# Revit family: QF_U-Line_UCRE427-SS01A___
name_source: partatom
category: Specialty Equipment
revit_build: Autodesk Revit 2018 (Build: 20190510_1515(x64)
units: mm (PartAtom-declared; Revit-internal decimal feet)

## family parameters
Always vertical = Yes
Cut with Voids When Loaded = No
Part Type = Normal
Room Calculation Point = No
Round Connector Dimension = Use Diameter
Shared = No
Work Plane-Based = No

## types (2) — shared parameters
Accessory = No
BTUH = 1421 W
CE Approved = Yes
Cooling Capacity = 0 kW
Cycle = 60 Hz
D5 = 5 mm  [stored 0.0164042 ft]
Depth Actual = 800 mm  [stored 2.62467 ft]
Description = Single solid door Refrigerator Basic line
Elec Connection Height = 2050 mm  [stored 6.72572 ft]
Electric power = 500 W
FL Amps = 5 A
Foodservice Equipment Identifier = Yes
Height Actual = 2050 mm  [stored 6.72572 ft]
Identify Quantity as Lot = No
Item Number = UCRE427-SS01A
Legs_R1 = 30 mm  [stored 0.0984252 ft]
Legs_R2 = 25 mm  [stored 0.082021 ft]
Length Actual = 700 mm  [stored 2.29659 ft]
Main switch integrated = No
Manufacturer = U-LINE
Mat_Case = QF_Stainless-Brushed
Mat_Clearance = QF_Clearance
Mat_Knob = QF_Stainless-Brushed
Mat_Legs = QF_Stainless-Brushed
Model = UCRE427-SS01A
Number of Poles = 1
Phase = 1
Potential Equalisation = Yes
Refrigerant Compressor Remote = No
URL Cutsheet = CRE427.PDF
URL Manufacturer = https://www.u-line.com
Volt Free Conn = No
Volts = 115 V
Weight = 130.00 kg
Weight in Pounds = 287

## per-type parameters (varying)
| type | LH | RH |
| UCRE427-SS01A_RH | No | Yes |
| UCRE427-SS01A_LH | Yes | No |

note: [stored X ft] marks values corroborated as IEEE doubles in the binary element streams (Revit-internal decimal feet)

## geometry (parser evidence)
native form markers: Sweep x19
no freeform markers — native parametric forms only
